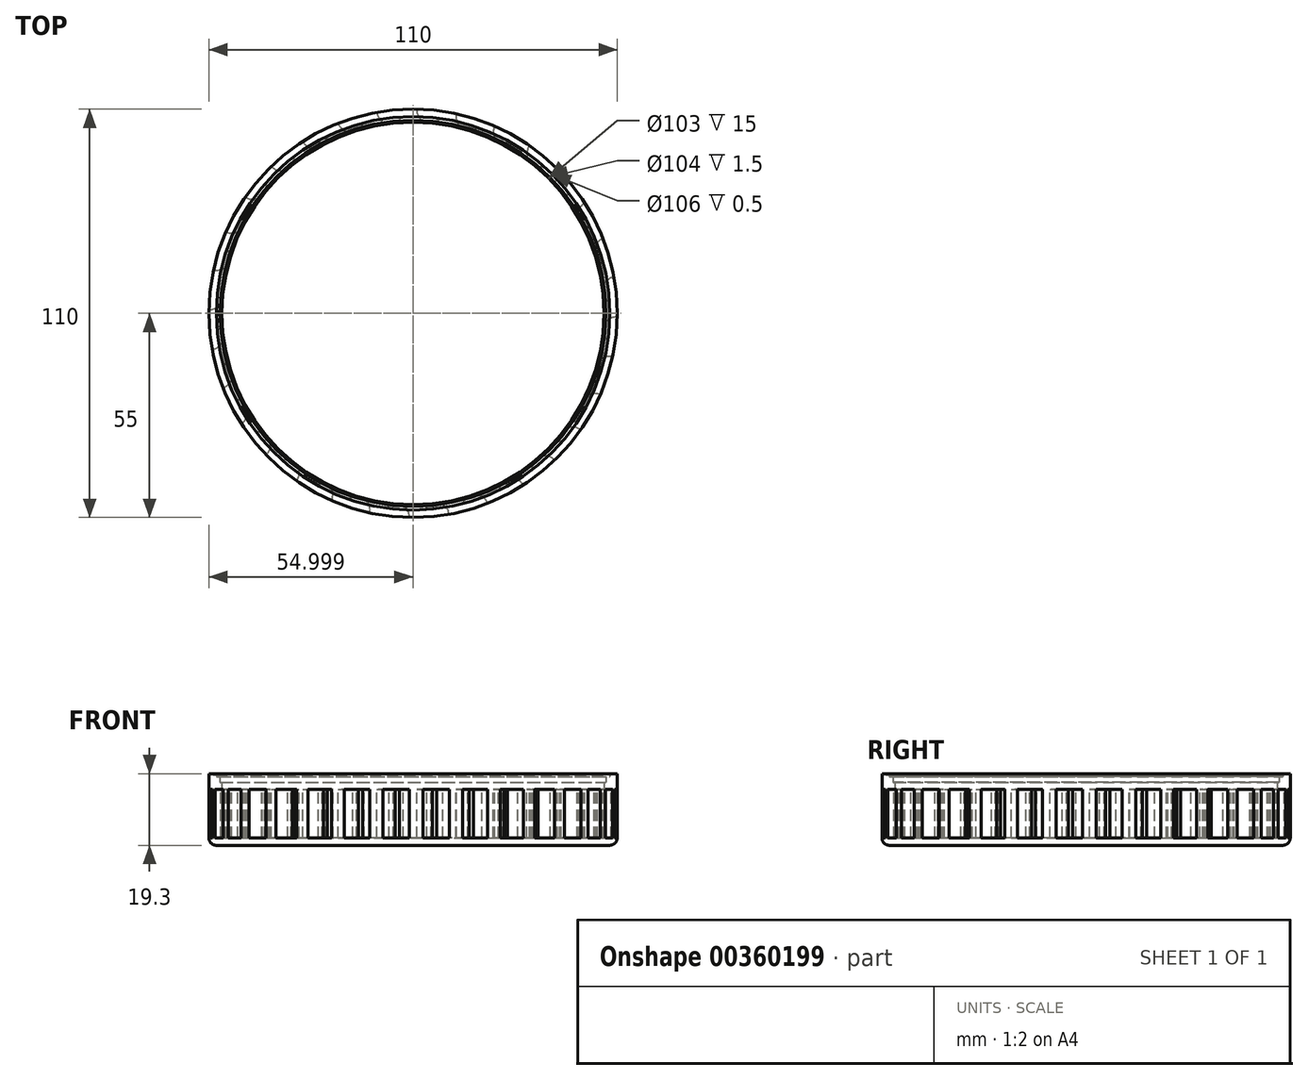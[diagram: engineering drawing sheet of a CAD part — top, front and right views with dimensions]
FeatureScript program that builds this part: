
annotation { "Feature Type Name" : "Feature", "Feature Type Description" : "" }
export const myFeature = defineFeature(function(context is Context, id is Id, definition is map)
    precondition{}
    {
        {
            var Q0;
            Q0=qCreatedBy(makeId("Front.planeOp"),FACE);
            var sketch = newSketch(context, id + "F0", { "sketchPlane" : qUnion([Q0])});
            skLineSegment(sketch, "E0", {"start": v(-18.95, 2.3) * mm, "end": v(-18.95, -12.7) * mm});
            skLineSegment(sketch, "E1", {"start": v(-18.95, -12.7) * mm, "end": v(-15.95, -12.7) * mm});
            skLineSegment(sketch, "E2", {"start": v(-17.95, 2.3) * mm, "end": v(-18.95, 2.3) * mm});
            skLineSegment(sketch, "E3", {"start": v(-17.95, 2.3) * mm, "end": v(-15.45, 2.3) * mm});
            skLineSegment(sketch, "E4", {"start": v(-15.45, 2.3) * mm, "end": v(-15.45, -10.7) * mm});
            skLineSegment(sketch, "E5", {"start": v(-15.45, 2.3) * mm, "end": v(-15.45, 0.3) * mm});
            skPoint(sketch, "E6", {"position": v(-15.45, 0.3) * mm});
            skLineSegment(sketch, "E7", {"start": v(-13.45, -12.7) * mm, "end": v(36.05, -12.7) * mm, "construction": true});
            skLineSegment(sketch, "E8", {"start": v(36.05, -12.7) * mm, "end": v(36.05, 12.3) * mm, "construction": true});
            skLineSegment(sketch, "E9", {"start": v(-18.95, 2.3) * mm, "end": v(-18.95, 4.3) * mm});
            skLineSegment(sketch, "E10", {"start": v(-18.95, 4.3) * mm, "end": v(-16.95, 4.3) * mm});
            skLineSegment(sketch, "E11", {"start": v(-16.95, 4.3) * mm, "end": v(-16.95, 2.3) * mm});
            skLineSegment(sketch, "E12", {"start": v(-15.95, -12.7) * mm, "end": v(36.05, -12.7) * mm});
            skLineSegment(sketch, "E13", {"start": v(36.05, -12.7) * mm, "end": v(36.05, -14.7) * mm});
            skLineSegment(sketch, "E14", {"start": v(36.05, -14.7) * mm, "end": v(-16.95, -14.7) * mm});
            skLineSegment(sketch, "E15", {"start": v(-18.95, -12.7) * mm, "end": v(-18.95, -12.7) * mm});
            skPoint(sketch, "E16.visualSharp", {"position": v(-18.95, -14.7) * mm});
            skArc(sketch, "E16.filletArc", {"start": v(-18.95, -12.7) * mm, "mid": v(-18.37, -14.1) * mm, "end": v(-16.95, -14.7) * mm});
            skPoint(sketch, "E17.newPointA", {"position": v(-15.45, -12.7) * mm});
            skPoint(sketch, "E17.newPointB", {"position": v(-18.95, -12.7) * mm});
            skLineSegment(sketch, "E18", {"start": v(-16.95, 4.3) * mm, "end": v(-16.95, 3.8) * mm});
            skLineSegment(sketch, "E19", {"start": v(-16.95, 3.8) * mm, "end": v(-15.95, 3.8) * mm});
            skLineSegment(sketch, "E20", {"start": v(-15.95, 3.8) * mm, "end": v(-15.95, 2.3) * mm});
            skLineSegment(sketch, "E21", {"start": v(-18.95, 4.3) * mm, "end": v(-18.95, 4.6) * mm});
            skArc(sketch, "E22", {"start": v(-18.95, 4.6) * mm, "mid": v(-17.96, 4.38) * mm, "end": v(-16.95, 4.3) * mm});
            skLineSegment(sketch, "E23", {"start": v(-15.45, -10.7) * mm, "end": v(-15.45, -12.7) * mm});
            skSolve(sketch);
        }
        {
            var Q0;
            Q0=makeQuery(id+"F0.imprint","IMPRINT",FACE,{"disambiguationData":[TD([[makeQuery(id+"F0.imprint","IMPRINT",EDGE,{"derivedFrom":sQuery(id+"F0.wireOp",EDGE,"E0")}),1.0]])]});
            var Q1;
            Q1=makeQuery(id+"F0.imprint","IMPRINT",FACE,{"disambiguationData":[TD([[makeQuery(id+"F0.imprint","IMPRINT",EDGE,{"derivedFrom":sQuery(id+"F0.wireOp",EDGE,"ivvwax1L-32Tc-sTfU-KpS2-KRKKGSkygf5M")}),-1.0]])]});
            var Q2;
            {var subQ0=sQuery(id+"F0.wireOp",EDGE,"E9");Q2=makeQuery(id+"F0.imprint","IMPRINT",FACE,{"disambiguationData":[TD([[makeQuery(id+"F0.imprint","IMPRINT",EDGE,{"derivedFrom":subQ0}),-1.0]])]});}
            var Q3;
            {var subQ1=sQuery(id+"F0.wireOp",EDGE,"E1");Q3=makeQuery(id+"F0.imprint","IMPRINT",FACE,{"disambiguationData":[TD([[makeQuery(id+"F0.imprint","IMPRINT",EDGE,{"derivedFrom":subQ1}),-1.0]])]});}
            var Q4;
            Q4=makeQuery(id+"F0.imprint","IMPRINT",FACE,{"disambiguationData":[TD([[makeQuery(id+"F0.imprint","IMPRINT",EDGE,{"derivedFrom":sQuery(id+"F0.wireOp",EDGE,"E10")}),1.0]])]});
            var Q5;
            {var subQ0=sQuery(id+"F0.wireOp",EDGE,"E11");Q5=makeQuery(id+"F0.imprint","IMPRINT",FACE,{"disambiguationData":[TD([[makeQuery(id+"F0.imprint","IMPRINT",EDGE,{"derivedFrom":subQ0}),1.0]])]});}
            var Q6;
            Q6=sQuery(id+"F0.wireOp",EDGE,"E8");
            revolve(context, id + "F1", {"entities" : qUnion([Q0, Q1, Q2, Q3, Q4, Q5]), "axis" : qUnion([Q6]), "revolveType" : RevolveType.FULL});
        }
        {
            var Q0;
            Q0=sQuery(id+"F0.wireOp",VERTEX,"E6");
            var Q1;
            Q1=sQuery(id+"F0.wireOp",EDGE,"E4");
            cPlane(context, id + "F2", {"entities" : qUnion([Q0, Q1]), "cplaneType" : CPlaneType.LINE_POINT, "offset" : 25 * mm, "width" : 150 * mm, "height" : 150 * mm});
        }
        {
            var Q0;
            Q0=qCreatedBy(id+"F2.planeOp",FACE);
            var sketch = newSketch(context, id + "F3", { "sketchPlane" : qUnion([Q0])});
            skCircle(sketch, "E24.0", {"center": v(36.05, 0) * mm, "radius": 55 * mm});
            skPoint(sketch, "E25.0", {"position": v(-18.95, 0) * mm});
            skPoint(sketch, "E26.0", {"position": v(-15.45, 0) * mm});
            skLineSegment(sketch, "E27", {"start": v(-18.95, 0) * mm, "end": v(-18.6, -6.24) * mm, "construction": true});
            skLineSegment(sketch, "E28", {"start": v(-18.95, 0) * mm, "end": v(-18.6, 6.24) * mm, "construction": true});
            skCircle(sketch, "E29", {"center": v(-18.6, -6.24) * mm, "radius": 3.55 * mm});
            skCircle(sketch, "E30", {"center": v(-18.6, 6.24) * mm, "radius": 3.55 * mm});
            skCircle(sketch, "E31.0", {"center": v(36.05, 0) * mm, "radius": 51.5 * mm});
            skSolve(sketch);
        }
        {
            var Q0;
            {var subQ0=sQuery(id+"F3.wireOp",EDGE,"E30");var subQ1=sQuery(id+"F3.wireOp",EDGE,"E24.0");var subQ2=makeQuery(id+"F3.imprint","INTERSECT",VERTEX,{"disambiguationData":[OD(0.0)],"derivedFrom":[subQ1,subQ0]});Q0=makeQuery(id+"F3.imprint","IMPRINT",FACE,{"disambiguationData":[TD([[makeQuery(id+"F3.imprint","IMPRINT",EDGE,{"disambiguationData":[TD([[subQ2,-1.0]])],"derivedFrom":subQ1}),1.0]])]});}
            extrude(context, id + "F4", {"entities" : qUnion([Q0]), "depth" : 13 * mm});
        }
        {
            var Q0;
            Q0=makeQuery(id+"F4.opExtrude","SWEPT_BODY",BODY,{"disambiguationData":[OSD([sQuery(id+"F3.wireOp",EDGE,"E24.0"),sQuery(id+"F3.wireOp",EDGE,"E29"),sQuery(id+"F3.wireOp",EDGE,"E30"),sQuery(id+"F3.wireOp",EDGE,"E31.0")])]});
            var Q1;
            Q1=sQuery(id+"F0.wireOp",EDGE,"E8");
            circularPattern(context, id + "F5", {"operationType" : NewBodyOperationType.REMOVE, "entities" : qUnion([Q0]), "axis" : qUnion([Q1]), "angle" : 360 * degree, "instanceCount" : 32, "equalSpace" : true});
        }
    });
